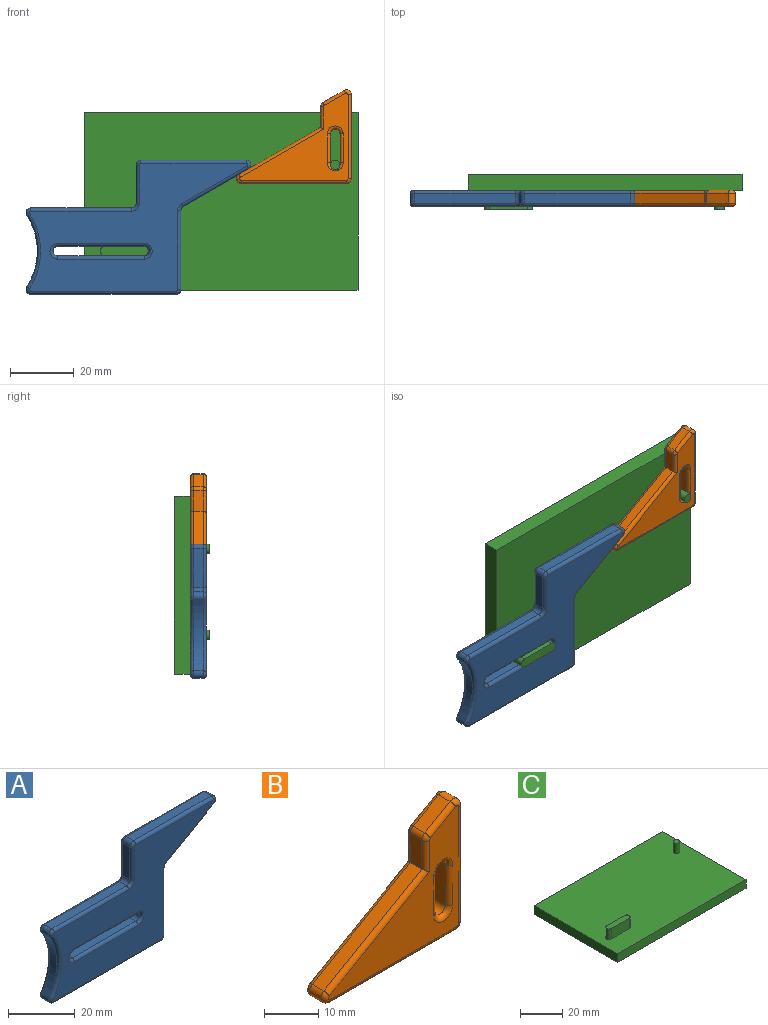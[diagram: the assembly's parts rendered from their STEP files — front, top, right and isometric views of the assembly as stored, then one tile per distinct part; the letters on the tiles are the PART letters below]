
ASSEMBLY  parts=3 mates=4
PART A: 56 faces, bbox 70.4x5x42 mm
  f0: plane 27x3mm, normal (0,0,1), area 81mm2, adj f1,f17,f50,f55
  f1: cylinder r=1.5mm len=3mm, axis (0,1,0), area 14.1mm2, adj f0,f2,f51,f53
  f2: plane 27x3mm, normal (0,0,-1), area 81mm2, adj f1,f17,f49,f52
  f3: cylinder r=20.54mm len=22.37mm, axis (0,1,0), area 71mm2, adj f4,f16,f20,f41
  f4: cylinder r=1.5mm len=3mm, axis (0,1,0), area 9.7mm2, adj f3,f5,f21,f39
  f5: plane 45.49x3mm, normal (0,0,-1), area 136.5mm2, adj f4,f6,f23,f37
  f6: cylinder r=1.5mm len=3mm, axis (0,1,0), area 7.1mm2, adj f5,f7,f25,f35
  f7: plane 24.63x3mm, normal (1,0,0), area 73.9mm2, adj f6,f8,f27,f34
  f8: cylinder r=1.5mm len=3mm, axis (0,1,0), area 4.7mm2, adj f7,f9,f29,f36
  f9: plane 20.38x11.77mm, normal (0.5,0,-0.87), area 70.6mm2, adj f8,f10,f31,f38
  f10: cylinder r=1.5mm len=3mm, axis (0,1,0), area 11.8mm2, adj f9,f11,f33,f40
  f11: plane 32.9x3mm, normal (0,0,1), area 98.7mm2, adj f10,f12,f32,f42
  f12: cylinder r=1.5mm len=3mm, axis (0,1,0), area 7.1mm2, adj f11,f13,f30,f44
  f13: plane 12x3mm, normal (-1,0,0), area 36mm2, adj f12,f14,f28,f46
  f14: cylinder r=1.5mm len=3mm, axis (0,1,0), area 7.1mm2, adj f13,f15,f26,f47
  f15: plane 31.47x3mm, normal (0,0,1), area 94.4mm2, adj f14,f16,f24,f45
  f16: cylinder r=1.5mm len=3mm, axis (0,1,0), area 9.7mm2, adj f3,f15,f22,f43
  f17: cylinder r=1.5mm len=3mm, axis (0,1,0), area 14.1mm2, adj f0,f2,f48,f54
  f18: plane 68.38x40mm, normal (0,-1,0), area 1287.7mm2, adj f34,f35,f36,f37,f38,f39,f40,f41
  f19: plane 68.38x40mm, normal (0,1,0), area 1287.7mm2, adj f20,f21,f22,f23,f24,f25,f26,f27
  f20: torus R=21.54mm, axis (0,-1,0), area 37.8mm2, adj f3,f19,f21,f22
  f21: torus R=0.5mm, axis (0,-1,0), area 3.8mm2, adj f4,f19,f20,f23
  f22: torus R=0.5mm, axis (0,-1,0), area 3.8mm2, adj f16,f19,f20,f24
  f23: cylinder r=1mm len=45.49mm, axis (1,0,0), area 71.5mm2, adj f5,f19,f21,f25
  f24: cylinder r=1mm len=31.47mm, axis (-1,0,0), area 49.4mm2, adj f15,f19,f22,f26
  f25: torus R=0.5mm, axis (0,-1,0), area 2.8mm2, adj f6,f19,f23,f27
  f26: torus R=2.5mm, axis (0,-1,0), area 4.6mm2, adj f14,f19,f24,f28
  f27: cylinder r=1mm len=24.63mm, axis (0,0,1), area 38.7mm2, adj f7,f19,f25,f29
  f28: cylinder r=1mm len=12mm, axis (0,0,-1), area 18.8mm2, adj f13,f19,f26,f30
  f29: torus R=2.5mm, axis (0,-1,0), area 3.1mm2, adj f8,f19,f27,f31
  f30: torus R=0.5mm, axis (0,-1,0), area 2.8mm2, adj f12,f19,f28,f32
  f31: cylinder r=1mm len=20.88mm, axis (0.87,0,0.5), area 37mm2, adj f9,f19,f29,f33
  f32: cylinder r=1mm len=32.9mm, axis (-1,0,0), area 51.7mm2, adj f11,f19,f30,f33
  f33: torus R=0.5mm, axis (0,-1,0), area 4.7mm2, adj f10,f19,f31,f32
  f34: cylinder r=1mm len=24.63mm, axis (0,0,-1), area 38.7mm2, adj f7,f18,f35,f36
  f35: torus R=0.5mm, axis (0,-1,0), area 2.8mm2, adj f6,f18,f34,f37
  f36: torus R=2.5mm, axis (0,-1,0), area 3.1mm2, adj f8,f18,f34,f38
  f37: cylinder r=1mm len=45.49mm, axis (-1,0,0), area 71.5mm2, adj f5,f18,f35,f39
  f38: cylinder r=1mm len=20.88mm, axis (-0.87,0,-0.5), area 37mm2, adj f9,f18,f36,f40
  f39: torus R=0.5mm, axis (0,-1,0), area 3.8mm2, adj f4,f18,f37,f41
  f40: torus R=0.5mm, axis (0,-1,0), area 4.7mm2, adj f10,f18,f38,f42
  f41: torus R=21.54mm, axis (0,-1,0), area 37.8mm2, adj f3,f18,f39,f43
  f42: cylinder r=1mm len=32.9mm, axis (1,0,0), area 51.7mm2, adj f11,f18,f40,f44
  f43: torus R=0.5mm, axis (0,-1,0), area 3.8mm2, adj f16,f18,f41,f45
  f44: torus R=0.5mm, axis (0,-1,0), area 2.8mm2, adj f12,f18,f42,f46
  f45: cylinder r=1mm len=31.47mm, axis (1,0,0), area 49.4mm2, adj f15,f18,f43,f47
  f46: cylinder r=1mm len=12mm, axis (0,0,1), area 18.8mm2, adj f13,f18,f44,f47
  f47: torus R=2.5mm, axis (0,-1,0), area 4.6mm2, adj f14,f18,f45,f46
  f48: torus R=2.5mm, axis (0,-1,0), area 9.2mm2, adj f17,f19,f49,f50
  f49: cylinder r=1mm len=27mm, axis (1,0,0), area 42.4mm2, adj f2,f19,f48,f51
  f50: cylinder r=1mm len=27mm, axis (-1,0,0), area 42.4mm2, adj f0,f19,f48,f51
  f51: torus R=2.5mm, axis (0,-1,0), area 9.2mm2, adj f1,f19,f49,f50
  f52: cylinder r=1mm len=27mm, axis (-1,0,0), area 42.4mm2, adj f2,f18,f53,f54
  f53: torus R=2.5mm, axis (0,-1,0), area 9.2mm2, adj f1,f18,f52,f55
  f54: torus R=2.5mm, axis (0,-1,0), area 9.2mm2, adj f17,f18,f52,f55
  f55: cylinder r=1mm len=27mm, axis (1,0,0), area 42.4mm2, adj f0,f18,f53,f54
PART B: 41 faces, bbox 35.9x5x29.3 mm
  f0: cylinder r=1.5mm len=3mm, axis (0,1,0), area 14.1mm2, adj f1,f12,f35,f39
  f1: plane 9x3mm, normal (1,0,0), area 27mm2, adj f0,f2,f33,f37
  f2: cylinder r=1.5mm len=3mm, axis (0,1,0), area 14.1mm2, adj f1,f12,f34,f38
  f3: plane 26.33x3mm, normal (1,0,0), area 79mm2, adj f4,f11,f16,f25
  f4: cylinder r=1.5mm len=3mm, axis (0,1,0), area 9.4mm2, adj f3,f5,f18,f27
  f5: plane 6.62x3.82mm, normal (-0.5,0,0.87), area 22.9mm2, adj f4,f6,f20,f29
  f6: cylinder r=1.5mm len=3mm, axis (0,1,0), area 4.7mm2, adj f5,f7,f22,f31
  f7: plane 6.46x3mm, normal (-1,0,0), area 19.4mm2, adj f6,f8,f23,f32
  f8: plane 25.55x14.75mm, normal (-0.5,0,0.87), area 88.5mm2, adj f7,f9,f21,f30
  f9: cylinder r=1.5mm len=3mm, axis (0,1,0), area 11.8mm2, adj f8,f10,f19,f28
  f10: plane 32.91x3mm, normal (0,0,-1), area 98.7mm2, adj f9,f11,f17,f26
  f11: cylinder r=1.5mm len=3mm, axis (0,1,0), area 7.1mm2, adj f3,f10,f15,f24
  f12: plane 9x3mm, normal (-1,0,0), area 27mm2, adj f0,f2,f36,f40
  f13: plane 33.91x27.33mm, normal (0,-1,0), area 349.6mm2, adj f24,f25,f26,f27,f28,f29,f30,f31
  f14: plane 33.91x27.33mm, normal (0,1,0), area 349.6mm2, adj f15,f16,f17,f18,f19,f20,f21,f22
  f15: torus R=0.5mm, axis (0,-1,0), area 2.8mm2, adj f11,f14,f16,f17
  f16: cylinder r=1mm len=26.33mm, axis (0,0,1), area 41.4mm2, adj f3,f14,f15,f18
  f17: cylinder r=1mm len=32.91mm, axis (1,0,0), area 51.7mm2, adj f10,f14,f15,f19
  f18: torus R=0.5mm, axis (0,-1,0), area 3.7mm2, adj f4,f14,f16,f20
  f19: torus R=0.5mm, axis (0,-1,0), area 4.7mm2, adj f9,f14,f17,f21
  f20: cylinder r=1mm len=7.12mm, axis (-0.87,0,-0.5), area 12mm2, adj f5,f14,f18,f22
  f21: cylinder r=1mm len=26.55mm, axis (-0.87,0,-0.5), area 46.7mm2, adj f8,f14,f19,f23
  f22: torus R=0.5mm, axis (0,-1,0), area 1.9mm2, adj f6,f14,f20,f23
  f23: cylinder r=1mm len=7.03mm, axis (0,0,-1), area 10.5mm2, adj f7,f14,f21,f22
  f24: torus R=0.5mm, axis (0,-1,0), area 2.8mm2, adj f11,f13,f25,f26
  f25: cylinder r=1mm len=26.33mm, axis (0,0,-1), area 41.4mm2, adj f3,f13,f24,f27
  f26: cylinder r=1mm len=32.91mm, axis (-1,0,0), area 51.7mm2, adj f10,f13,f24,f28
  f27: torus R=0.5mm, axis (0,-1,0), area 3.7mm2, adj f4,f13,f25,f29
  f28: torus R=0.5mm, axis (0,-1,0), area 4.7mm2, adj f9,f13,f26,f30
  f29: cylinder r=1mm len=7.12mm, axis (0.87,0,0.5), area 12mm2, adj f5,f13,f27,f31
  f30: cylinder r=1mm len=26.55mm, axis (0.87,0,0.5), area 46.7mm2, adj f8,f13,f28,f32
  f31: torus R=0.5mm, axis (0,-1,0), area 1.9mm2, adj f6,f13,f29,f32
  f32: cylinder r=1mm len=7.03mm, axis (0,0,1), area 10.5mm2, adj f7,f13,f30,f31
  f33: cylinder r=1mm len=9mm, axis (0,0,1), area 14.1mm2, adj f1,f14,f34,f35
  f34: torus R=2.5mm, axis (0,-1,0), area 9.2mm2, adj f2,f14,f33,f36
  f35: torus R=2.5mm, axis (0,-1,0), area 9.2mm2, adj f0,f14,f33,f36
  f36: cylinder r=1mm len=9mm, axis (0,0,-1), area 14.1mm2, adj f12,f14,f34,f35
  f37: cylinder r=1mm len=9mm, axis (0,0,-1), area 14.1mm2, adj f1,f13,f38,f39
  f38: torus R=2.5mm, axis (0,-1,0), area 9.2mm2, adj f2,f13,f37,f40
  f39: torus R=2.5mm, axis (0,-1,0), area 9.2mm2, adj f0,f13,f37,f40
  f40: cylinder r=1mm len=9mm, axis (0,0,1), area 14.1mm2, adj f12,f13,f38,f39
PART C: 13 faces, bbox 85.6x55.7x11 mm
  f0: plane 12x6mm, normal (0,1,0), area 72mm2, adj f1,f3,f4,f11
  f1: cylinder r=1.5mm len=6mm, axis (0,0,-1), area 28.3mm2, adj f0,f2,f4,f11
  f2: plane 12x6mm, normal (0,-1,0), area 72mm2, adj f1,f3,f4,f11
  f3: cylinder r=1.5mm len=6mm, axis (0,0,-1), area 28.3mm2, adj f0,f2,f4,f11
  f4: plane 15x3mm, normal (0,0,1), area 43.1mm2, adj f0,f1,f2,f3
  f5: cylinder r=1.5mm len=6mm, axis (0,0,-1), area 56.5mm2, adj f6,f11
  f6: plane 3x3mm, normal (0,0,1), area 7.1mm2, adj f5
  f7: plane 85.63x5mm, normal (0,1,0), area 428.2mm2, adj f8,f10,f11,f12
  f8: plane 55.7x5mm, normal (-1,0,0), area 278.5mm2, adj f7,f9,f11,f12
  f9: plane 85.63x5mm, normal (0,-1,0), area 428.2mm2, adj f8,f10,f11,f12
  f10: plane 55.7x5mm, normal (1,0,0), area 278.5mm2, adj f7,f9,f11,f12
  f11: plane 85.63x55.7mm, normal (0,0,1), area 4719.4mm2, adj f0,f1,f2,f3,f5,f7,f8,f9
  f12: plane 85.63x55.7mm, normal (0,0,-1), area 4769.5mm2, adj f7,f8,f9,f10
PLACE A t=(-62.81,0,-29.21)mm
PLACE B t=(30.46,0,5.46)mm
PLACE C rot(axis=(1,0,0),90deg) t=(-30.54,5,-15.71)mm
MATE planar A.f2 <-> C.f0  axis (0,0,-1) through (-37.81,-2.5,-14.21)mm
MATE planar B.f8 <-> A.f9  axis (-0.5,0,0.87) through (18.08,-2.5,15.63)mm
MATE planar A.f16 <-> C.f11  axis (0,1,0) through (-59.8,0,-3.71)mm
MATE planar B.f14 <-> C.f11  axis (0,1,0) through (32.96,0,11.96)mm
